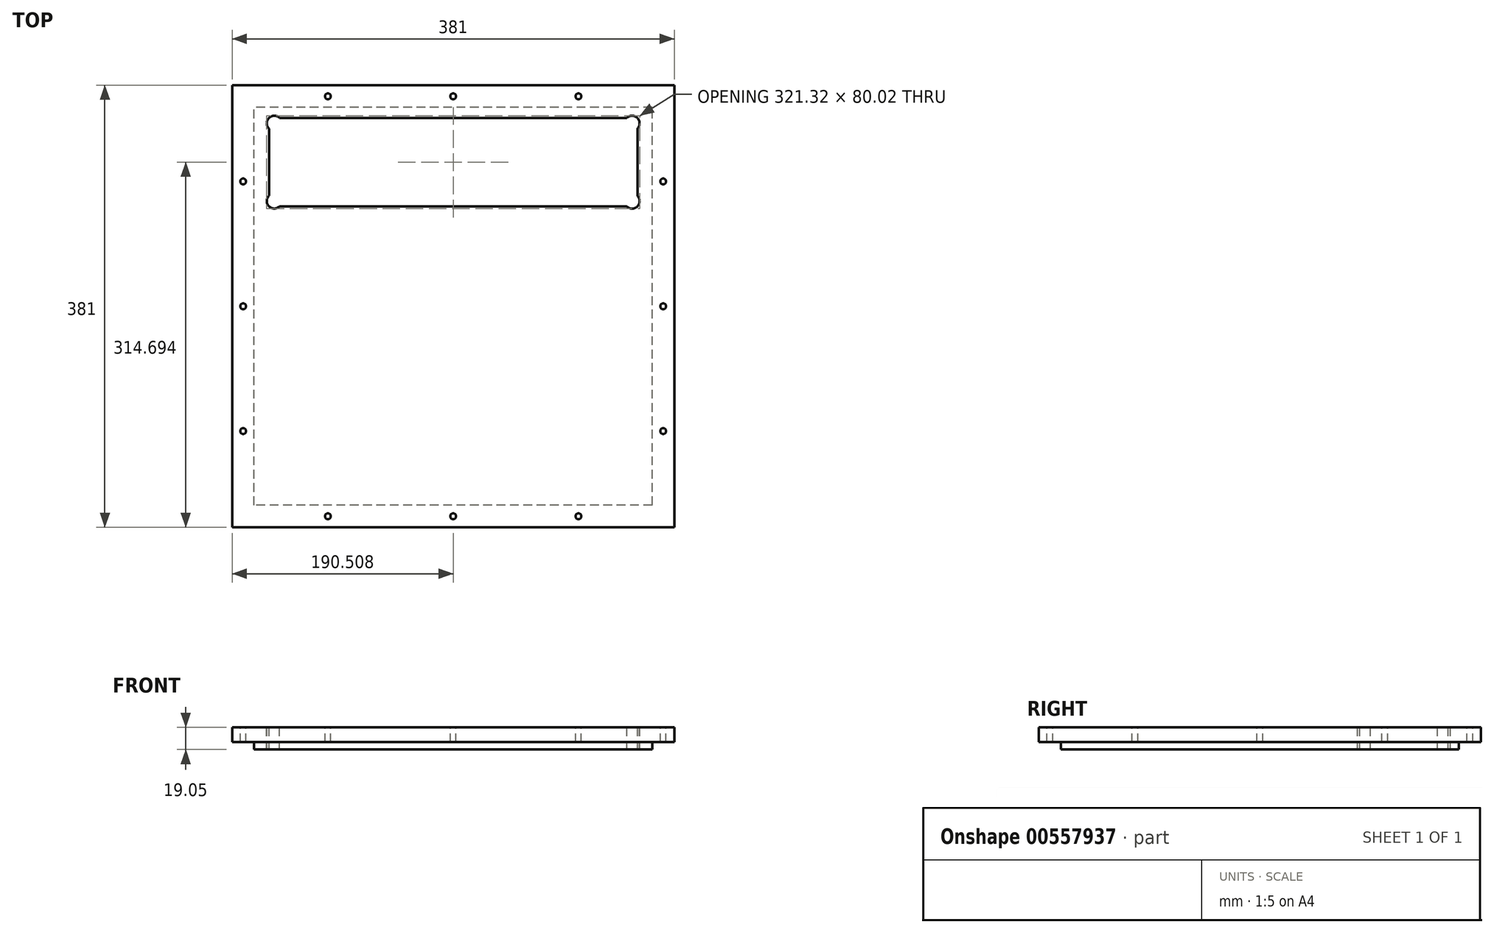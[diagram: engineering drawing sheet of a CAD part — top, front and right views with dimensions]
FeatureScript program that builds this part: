
annotation { "Feature Type Name" : "Feature", "Feature Type Description" : "" }
export const myFeature = defineFeature(function(context is Context, id is Id, definition is map)
    precondition{}
    {
        {
            var Q0;
            Q0=qCreatedBy(makeId("Top.planeOp"),FACE);
            var sketch = newSketch(context, id + "F0", { "sketchPlane" : qUnion([Q0])});
            skLineSegment(sketch, "E0.bottom", {"start": v(30.48, -406.4) * mm, "end": v(411.48, -406.4) * mm});
            skLineSegment(sketch, "E0.top", {"start": v(30.48, -25.4) * mm, "end": v(411.48, -25.4) * mm});
            skLineSegment(sketch, "E0.left", {"start": v(30.48, -406.4) * mm, "end": v(30.48, -25.4) * mm});
            skLineSegment(sketch, "E0.right", {"start": v(411.48, -406.4) * mm, "end": v(411.48, -25.4) * mm});
            skPoint(sketch, "E0.middle", {"position": v(220.98, -215.9) * mm});
            skLineSegment(sketch, "E1", {"start": v(62.23, -120.6) * mm, "end": v(62.23, -62.8) * mm});
            skLineSegment(sketch, "E2", {"start": v(71.42, -53.6) * mm, "end": v(370.54, -53.6) * mm});
            skLineSegment(sketch, "E3", {"start": v(379.73, -120.6) * mm, "end": v(379.73, -62.8) * mm});
            skLineSegment(sketch, "E4", {"start": v(71.42, -129.8) * mm, "end": v(370.54, -129.8) * mm});
            skArc(sketch, "E5.trimOffspring", {"start": v(62.29, -53.54) * mm, "mid": v(62.23, -53.6) * mm, "end": v(62.17, -53.66) * mm});
            skLineSegment(sketch, "E6.bottom", {"start": v(392.43, -387.35) * mm, "end": v(49.53, -387.35) * mm});
            skLineSegment(sketch, "E6.top", {"start": v(392.43, -44.45) * mm, "end": v(49.53, -44.45) * mm});
            skLineSegment(sketch, "E6.left", {"start": v(392.43, -387.35) * mm, "end": v(392.43, -44.45) * mm});
            skLineSegment(sketch, "E6.right", {"start": v(49.53, -387.35) * mm, "end": v(49.53, -44.45) * mm});
            skCircle(sketch, "E7", {"center": v(220.98, -34.93) * mm, "radius": 2.5 * mm});
            skPoint(sketch, "E8.endSnap0", {"position": v(30.48, -215.9) * mm});
            skCircle(sketch, "E9.MirrorC", {"center": v(40, -215.9) * mm, "radius": 2.5 * mm});
            skCircle(sketch, "E10.MirrorC", {"center": v(40, -108.29) * mm, "radius": 2.5 * mm});
            skCircle(sketch, "E11.MirrorC", {"center": v(113.03, -34.93) * mm, "radius": 2.5 * mm});
            skCircle(sketch, "E12.MirrorC", {"center": v(220.98, -396.88) * mm, "radius": 2.5 * mm});
            skCircle(sketch, "E13.MirrorC", {"center": v(113.03, -396.88) * mm, "radius": 2.5 * mm});
            skCircle(sketch, "E14.MirrorC", {"center": v(40, -323.51) * mm, "radius": 2.5 * mm});
            skCircle(sketch, "E15.MirrorC", {"center": v(328.93, -34.93) * mm, "radius": 2.5 * mm});
            skCircle(sketch, "E16.MirrorC", {"center": v(401.96, -108.29) * mm, "radius": 2.5 * mm});
            skCircle(sketch, "E17.MirrorC", {"center": v(401.96, -215.9) * mm, "radius": 2.5 * mm});
            skCircle(sketch, "E18.MirrorC", {"center": v(401.96, -323.51) * mm, "radius": 2.5 * mm});
            skCircle(sketch, "E19.MirrorC", {"center": v(328.93, -396.88) * mm, "radius": 2.5 * mm});
            skArc(sketch, "E20.MirrorCS", {"start": v(379.73, -62.8) * mm, "mid": v(379.72, -53.6) * mm, "end": v(370.54, -53.6) * mm});
            skArc(sketch, "E21.MirrorCS", {"start": v(62.23, -62.8) * mm, "mid": v(62.23, -53.6) * mm, "end": v(71.42, -53.6) * mm});
            skArc(sketch, "E22.MirrorCS", {"start": v(62.23, -120.6) * mm, "mid": v(62.25, -129.78) * mm, "end": v(71.42, -129.8) * mm});
            skArc(sketch, "E23.MirrorCS", {"start": v(379.73, -120.6) * mm, "mid": v(379.75, -129.81) * mm, "end": v(370.54, -129.8) * mm});
            skSolve(sketch);
        }
        {
            var Q0;
            Q0=makeQuery(id+"F0.imprint","IMPRINT",FACE,{"disambiguationData":[TD([[makeQuery(id+"F0.imprint","IMPRINT",EDGE,{"derivedFrom":sQuery(id+"F0.wireOp",EDGE,"E0.bottom")}),1.0]])]});
            extrude(context, id + "F1", {"entities" : qUnion([Q0]), "depth" : -12.7 * mm, "offsetDistance" : 25.4 * mm});
        }
        {
            var Q0;
            Q0=makeQuery(id+"F0.imprint","IMPRINT",FACE,{"disambiguationData":[TD([[makeQuery(id+"F0.imprint","IMPRINT",EDGE,{"derivedFrom":sQuery(id+"F0.wireOp",EDGE,"E1")}),1.0]])]});
            extrude(context, id + "F2", {"entities" : qUnion([Q0]), "operationType" : NewBodyOperationType.ADD, "depth" : -19.05 * mm, "offsetDistance" : 25.4 * mm});
        }
    });
